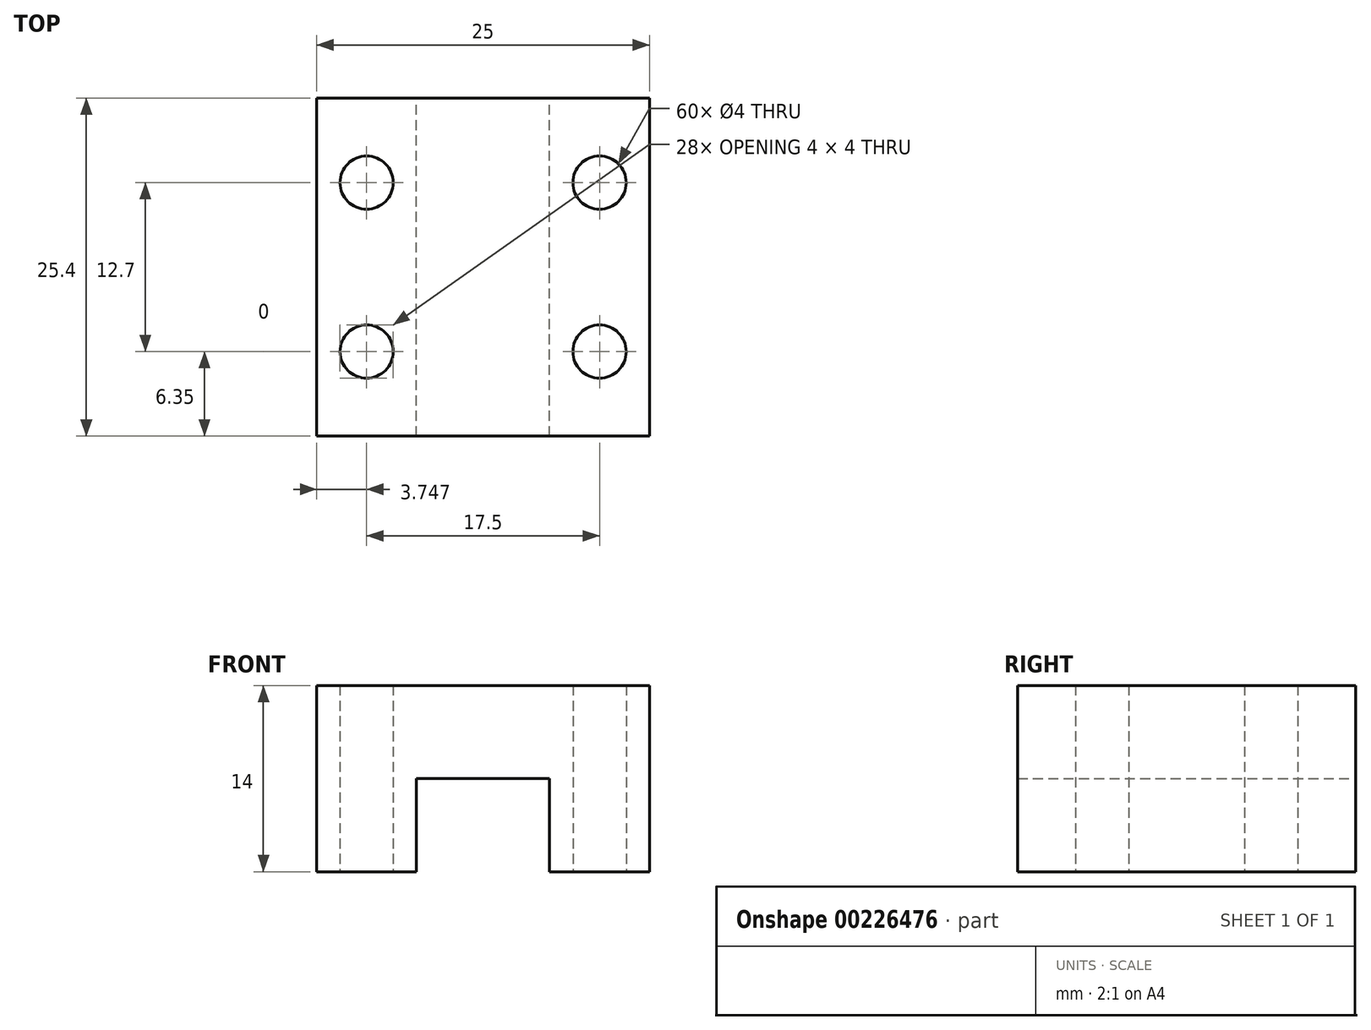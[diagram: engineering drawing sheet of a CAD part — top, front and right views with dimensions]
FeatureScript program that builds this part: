
annotation { "Feature Type Name" : "Feature", "Feature Type Description" : "" }
export const myFeature = defineFeature(function(context is Context, id is Id, definition is map)
    precondition{}
    {
        {
            var Q0;
            Q0=qCreatedBy(makeId("Front.planeOp"),FACE);
            var sketch = newSketch(context, id + "F0", { "sketchPlane" : qUnion([Q0])});
            skLineSegment(sketch, "E0", {"start": v(-11.98, 0) * mm, "end": v(-11.98, 14) * mm});
            skLineSegment(sketch, "E1", {"start": v(-11.98, 14) * mm, "end": v(13.02, 14) * mm});
            skLineSegment(sketch, "E2", {"start": v(13.02, 14) * mm, "end": v(13.02, 0) * mm});
            skLineSegment(sketch, "E3", {"start": v(13.02, 0) * mm, "end": v(5.52, 0) * mm});
            skLineSegment(sketch, "E4", {"start": v(5.52, 0) * mm, "end": v(5.52, 7) * mm});
            skLineSegment(sketch, "E5", {"start": v(5.52, 7) * mm, "end": v(-4.48, 7) * mm});
            skLineSegment(sketch, "E6", {"start": v(-4.48, 7) * mm, "end": v(-4.48, 0) * mm});
            skLineSegment(sketch, "E7", {"start": v(-4.48, 0) * mm, "end": v(-11.98, 0) * mm});
            skSolve(sketch);
        }
        {
            var Q0;
            Q0 = qSketchRegion(id + "F0", true);
            extrude(context, id + "F1", {"entities" : qUnion([Q0]), "depth" : 25.4 * mm});
        }
        {
            var Q0;
            Q0=makeQuery(id+"F1.opExtrude","SWEPT_FACE",FACE,{"disambiguationData":[OSD([sQuery(id+"F0.wireOp",EDGE,"E3")])]});
            var sketch = newSketch(context, id + "F2", { "sketchPlane" : qUnion([Q0])});
            skCircle(sketch, "E8", {"center": v(9.27, 19.05) * mm, "radius": 2 * mm});
            skCircle(sketch, "E9", {"center": v(9.27, 6.35) * mm, "radius": 2 * mm});
            skCircle(sketch, "E10", {"center": v(-8.23, 6.35) * mm, "radius": 2 * mm});
            skCircle(sketch, "E11", {"center": v(-8.23, 19.05) * mm, "radius": 2 * mm});
            skLineSegment(sketch, "E12", {"start": v(9.27, 19.05) * mm, "end": v(9.27, 25.4) * mm});
            skLineSegment(sketch, "E13", {"start": v(9.27, 6.35) * mm, "end": v(9.27, 0) * mm});
            skSolve(sketch);
        }
        {
            var Q0;
            Q0 = qSketchRegion(id + "F2", true);
            extrude(context, id + "F3", {"entities" : qUnion([Q0]), "operationType" : NewBodyOperationType.REMOVE, "endBound" : BoundingType.THROUGH_ALL, "oppositeDirection" : true, "depth" : 25.4 * mm});
        }
    });
